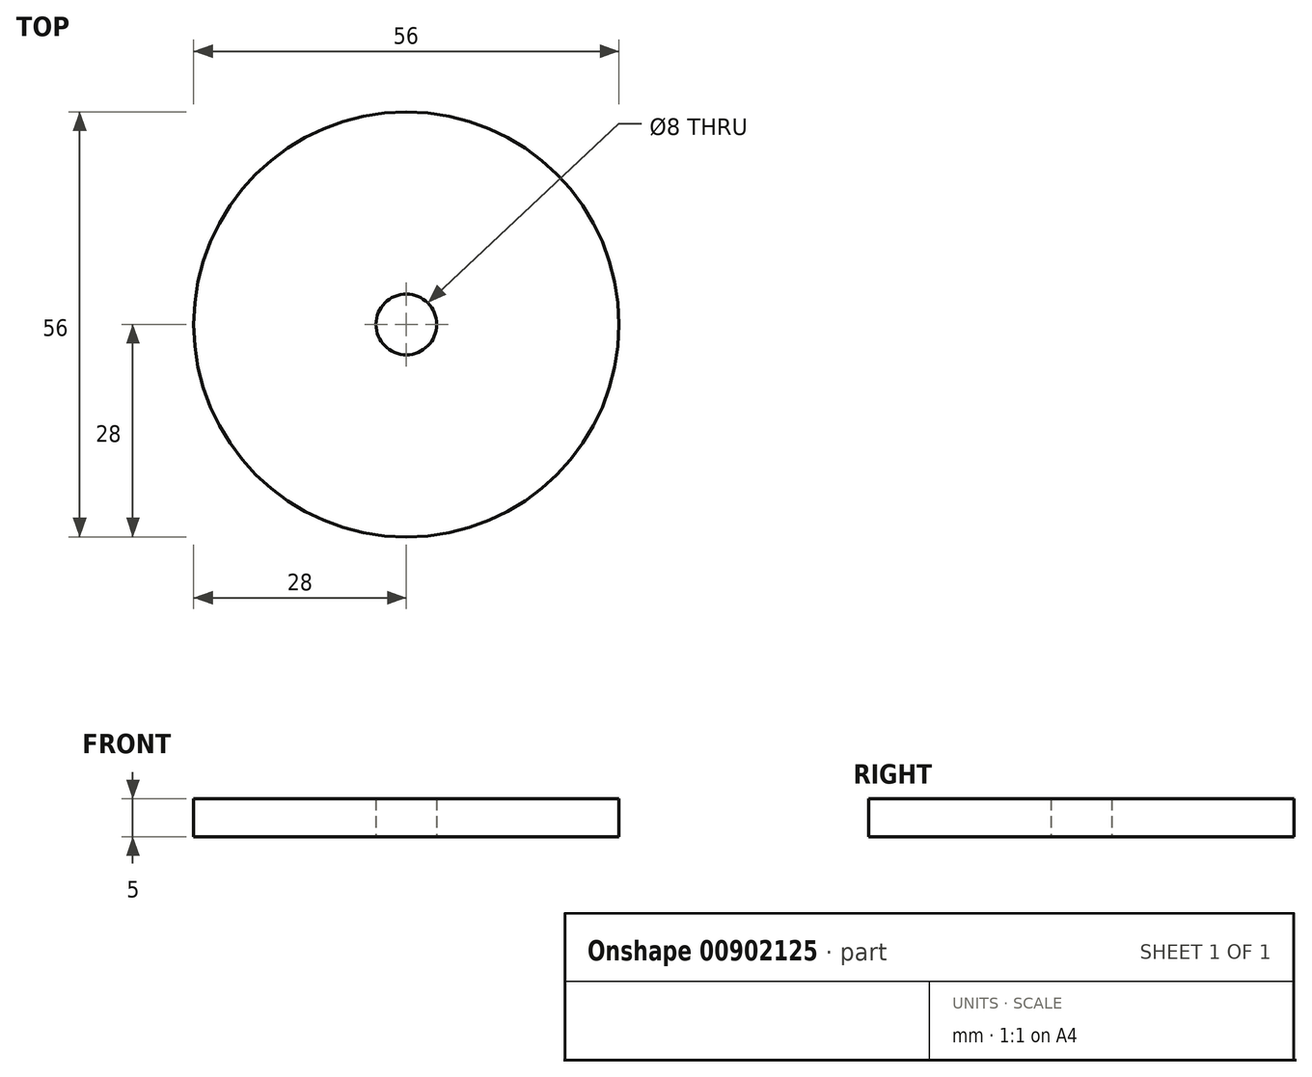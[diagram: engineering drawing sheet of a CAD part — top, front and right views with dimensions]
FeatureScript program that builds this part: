
annotation { "Feature Type Name" : "Feature", "Feature Type Description" : "" }
export const myFeature = defineFeature(function(context is Context, id is Id, definition is map)
    precondition{}
    {
        {
            var Q0;
            Q0=qCreatedBy(makeId("Top.planeOp"),FACE);
            var sketch = newSketch(context, id + "F0", { "sketchPlane" : qUnion([Q0])});
            skCircle(sketch, "E0", {"center": v(0, 0) * mm, "radius": 4 * mm});
            skCircle(sketch, "E1", {"center": v(0, 0) * mm, "radius": 28 * mm});
            skSolve(sketch);
        }
        {
            var Q0;
            Q0=makeQuery(id+"F0.imprint","IMPRINT",FACE,{"disambiguationData":[TD([[makeQuery(id+"F0.imprint","IMPRINT",EDGE,{"derivedFrom":sQuery(id+"F0.wireOp",EDGE,"E0")}),-1.0]])]});
            extrude(context, id + "F1", {"entities" : qUnion([Q0]), "depth" : 5 * mm, "offsetDistance" : 25 * mm});
        }
    });
